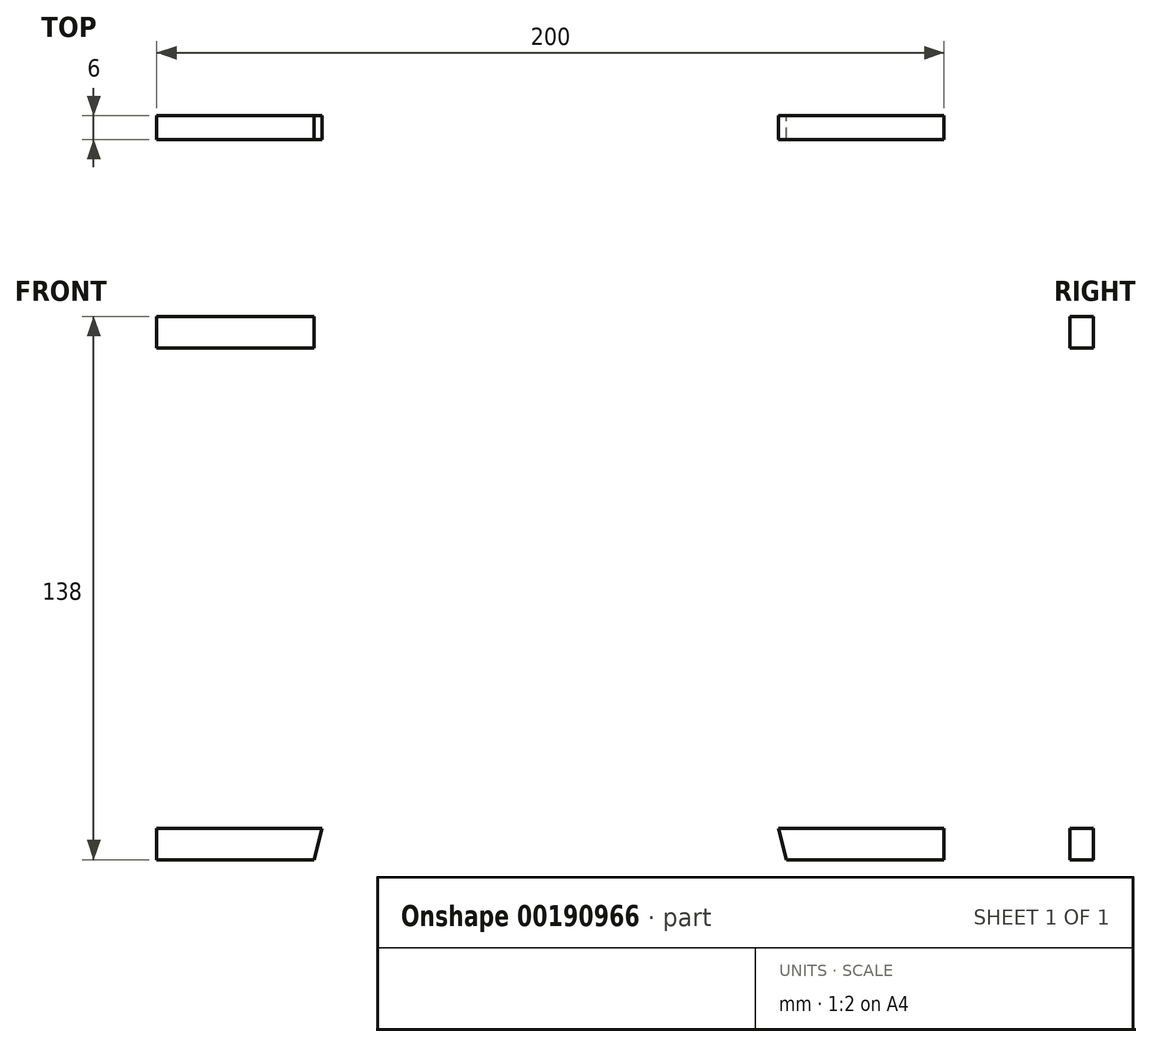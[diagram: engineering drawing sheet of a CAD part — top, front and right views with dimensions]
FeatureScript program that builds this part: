
annotation { "Feature Type Name" : "Feature", "Feature Type Description" : "" }
export const myFeature = defineFeature(function(context is Context, id is Id, definition is map)
    precondition{}
    {
        {
            var Q0;
            Q0=qCreatedBy(makeId("Front.planeOp"),FACE);
            var sketch = newSketch(context, id + "F0", { "sketchPlane" : qUnion([Q0])});
            skLineSegment(sketch, "E0.bottom", {"start": v(0, 0) * mm, "end": v(200, 0) * mm});
            skLineSegment(sketch, "E0.top", {"start": v(0, 130) * mm, "end": v(200, 130) * mm});
            skLineSegment(sketch, "E0.left", {"start": v(0, 0) * mm, "end": v(0, 130) * mm});
            skLineSegment(sketch, "E0.right", {"start": v(200, 0) * mm, "end": v(200, 130) * mm});
            skCircle(sketch, "E1", {"center": v(100, 65) * mm, "radius": 15.15 * mm});
            skCircle(sketch, "E2", {"center": v(61.03, 87.5) * mm, "radius": 5 * mm});
            skCircle(sketch, "E3", {"center": v(138.97, 42.5) * mm, "radius": 5 * mm});
            skLineSegment(sketch, "E4.bottom", {"start": v(100, 49.85) * mm, "end": v(200, 49.85) * mm});
            skLineSegment(sketch, "E4.top", {"start": v(100, 80.15) * mm, "end": v(200, 80.15) * mm});
            skLineSegment(sketch, "E4.left", {"start": v(100, 49.85) * mm, "end": v(100, 80.15) * mm});
            skLineSegment(sketch, "E4.right", {"start": v(200, 49.85) * mm, "end": v(200, 80.15) * mm});
            skLineSegment(sketch, "E5.bottom", {"start": v(200, 39.7) * mm, "end": v(159.7, 39.7) * mm});
            skLineSegment(sketch, "E5.top", {"start": v(200, 90.3) * mm, "end": v(159.7, 90.3) * mm});
            skLineSegment(sketch, "E5.left", {"start": v(200, 39.7) * mm, "end": v(200, 90.3) * mm});
            skLineSegment(sketch, "E5.right", {"start": v(159.7, 39.7) * mm, "end": v(159.7, 90.3) * mm});
            skCircle(sketch, "E6", {"center": v(180, 110) * mm, "radius": 5 * mm});
            skCircle(sketch, "E7", {"center": v(180, 20) * mm, "radius": 5 * mm});
            skCircle(sketch, "E8", {"center": v(20, 110) * mm, "radius": 5 * mm});
            skCircle(sketch, "E9", {"center": v(20, 20) * mm, "radius": 5 * mm});
            skCircle(sketch, "E10", {"center": v(180, 80) * mm, "radius": 5 * mm});
            skCircle(sketch, "E11", {"center": v(180, 50) * mm, "radius": 5 * mm});
            skLineSegment(sketch, "E12", {"start": v(61.03, 87.5) * mm, "end": v(100, 65) * mm});
            skLineSegment(sketch, "E13", {"start": v(100, 65) * mm, "end": v(138.97, 42.5) * mm});
            skLineSegment(sketch, "E14.bottom", {"start": v(0, -8) * mm, "end": v(40, -8) * mm});
            skLineSegment(sketch, "E14.top", {"start": v(0, 0) * mm, "end": v(40, 0) * mm});
            skLineSegment(sketch, "E14.left", {"start": v(0, -8) * mm, "end": v(0, 0) * mm});
            skLineSegment(sketch, "E14.right", {"start": v(40, -8) * mm, "end": v(40, 0) * mm});
            skLineSegment(sketch, "E15.bottom", {"start": v(200, -8) * mm, "end": v(160, -8) * mm});
            skLineSegment(sketch, "E15.top", {"start": v(200, 0) * mm, "end": v(160, 0) * mm});
            skLineSegment(sketch, "E15.left", {"start": v(200, -8) * mm, "end": v(200, 0) * mm});
            skLineSegment(sketch, "E15.right", {"start": v(160, -8) * mm, "end": v(160, 0) * mm});
            skLineSegment(sketch, "E16", {"start": v(40, -8) * mm, "end": v(42, 0) * mm});
            skLineSegment(sketch, "E17", {"start": v(160, -8) * mm, "end": v(158, 0) * mm});
            skLineSegment(sketch, "E18.bottom", {"start": v(0, 122) * mm, "end": v(40, 122) * mm});
            skLineSegment(sketch, "E18.top", {"start": v(0, 130) * mm, "end": v(40, 130) * mm});
            skLineSegment(sketch, "E18.left", {"start": v(0, 122) * mm, "end": v(0, 130) * mm});
            skLineSegment(sketch, "E18.right", {"start": v(40, 122) * mm, "end": v(40, 130) * mm});
            skLineSegment(sketch, "E19.bottom", {"start": v(200, 122) * mm, "end": v(160, 122) * mm});
            skLineSegment(sketch, "E19.top", {"start": v(200, 130) * mm, "end": v(160, 130) * mm});
            skLineSegment(sketch, "E19.left", {"start": v(200, 122) * mm, "end": v(200, 130) * mm});
            skLineSegment(sketch, "E19.right", {"start": v(160, 122) * mm, "end": v(160, 130) * mm});
            skLineSegment(sketch, "E20", {"start": v(40, 122) * mm, "end": v(42, 130) * mm});
            skLineSegment(sketch, "E21", {"start": v(160, 122) * mm, "end": v(158, 130) * mm});
            skSolve(sketch);
        }
        {
            var Q0;
            {var subQ22=sQuery(id+"F0.wireOp",EDGE,"E0.left");Q0=makeQuery(id+"F0.imprint","IMPRINT",FACE,{"disambiguationData":[TD([[makeQuery(id+"F0.imprint","IMPRINT",EDGE,{"derivedFrom":subQ22}),-1.0]])]});}
            var Q1;
            Q1=makeQuery(id+"F0.imprint","IMPRINT",FACE,{"disambiguationData":[TD([[makeQuery(id+"F0.imprint","IMPRINT",EDGE,{"derivedFrom":sQuery(id+"F0.wireOp",EDGE,"0B5afn8G-h0W6-BFAm-Bf3q-YGjXgToWp8EH.bottom")}),1.0]])]});
            var Q2;
            {var subQ0=sQuery(id+"F0.wireOp",EDGE,"JDXt8s4e-69hV-gc9z-V2TI-54T1ls7XA3z5.left");Q2=makeQuery(id+"F0.imprint","IMPRINT",FACE,{"disambiguationData":[TD([[makeQuery(id+"F0.imprint","IMPRINT",EDGE,{"derivedFrom":subQ0}),-1.0]])]});}
            var Q3;
            {var subQ0=sQuery(id+"F0.wireOp",EDGE,"JDXt8s4e-69hV-gc9z-V2TI-54T1ls7XA3z5.right");Q3=makeQuery(id+"F0.imprint","IMPRINT",FACE,{"disambiguationData":[TD([[makeQuery(id+"F0.imprint","IMPRINT",EDGE,{"derivedFrom":subQ0}),1.0]])]});}
            var Q4;
            Q4=makeQuery(id+"F0.imprint","IMPRINT",FACE,{"disambiguationData":[TD([[makeQuery(id+"F0.imprint","IMPRINT",EDGE,{"derivedFrom":sQuery(id+"F0.wireOp",EDGE,"E14.bottom")}),1.0]])]});
            var Q5;
            Q5=makeQuery(id+"F0.imprint","IMPRINT",FACE,{"disambiguationData":[TD([[makeQuery(id+"F0.imprint","IMPRINT",EDGE,{"derivedFrom":sQuery(id+"F0.wireOp",EDGE,"E15.bottom")}),-1.0]])]});
            var Q6;
            {var subQ0=sQuery(id+"F0.wireOp",EDGE,"E14.right");Q6=makeQuery(id+"F0.imprint","IMPRINT",FACE,{"disambiguationData":[TD([[makeQuery(id+"F0.imprint","IMPRINT",EDGE,{"derivedFrom":subQ0}),-1.0]])]});}
            var Q7;
            {var subQ0=sQuery(id+"F0.wireOp",EDGE,"E15.right");Q7=makeQuery(id+"F0.imprint","IMPRINT",FACE,{"disambiguationData":[TD([[makeQuery(id+"F0.imprint","IMPRINT",EDGE,{"derivedFrom":subQ0}),1.0]])]});}
            extrude(context, id + "F1", {"entities" : qUnion([Q0, Q1, Q2, Q3, Q4, Q5, Q6, Q7]), "depth" : 6 * mm});
        }
    });
